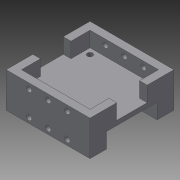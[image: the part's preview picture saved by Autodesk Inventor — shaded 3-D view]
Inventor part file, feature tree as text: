
AUTODESK INVENTOR PART (.ipt)
format: ipt  version: 2015 (Build 190159000, 159)  size: 162,816 bytes
history: native  units: in
note: dims shown in document units (in); Inventor stores cm internally (conversion verified against a paired STEP export)
features: extrude x6, sketch x6
ambient origin geometry x8: Origin, YZ Plane, XZ Plane, XY Plane, X Axis, Y Axis, Z Axis, Center Point
bodies: Solid1 (feature_tree)
feature tree (12):
  extrude  "Extrusion1"  Depth=0.15in TaperAngle=0.0deg
  extrude  "Extrusion2"  Depth=2.2441in
  extrude  "Extrusion3"  Depth=0.25in
  extrude  "Extrusion4"  Depth=1.6535in
  extrude  "Extrusion5"  Depth=1.25in
  extrude  "Extrusion6"  Depth=1.0in TaperAngle=0.0deg
  sketch  "Sketch1"  dims[d0=0.5in d1=0.0in d2=0.15in d3=0.0in]
  sketch  "Sketch2"  dims[d4=0.5in d5=0.0in d6=2.2441in]
  sketch  "Sketch3"  dims[d7=2.2441in d8=0.25in]
  sketch  "Sketch4"  dims[d10=1.6535in d38=0.1772in]
  sketch  "Sketch5"  dims[d39=0.1772in d41=1.25in]
  sketch  "Sketch6"  dims[d42=0.4in d43=1.0in d44=0.0in d45=0.1772in d46=1.8559in d47=1.8559in d48=0.5in d49=0.0in d51=0.5in d52=0.0in d53=1.0in]
